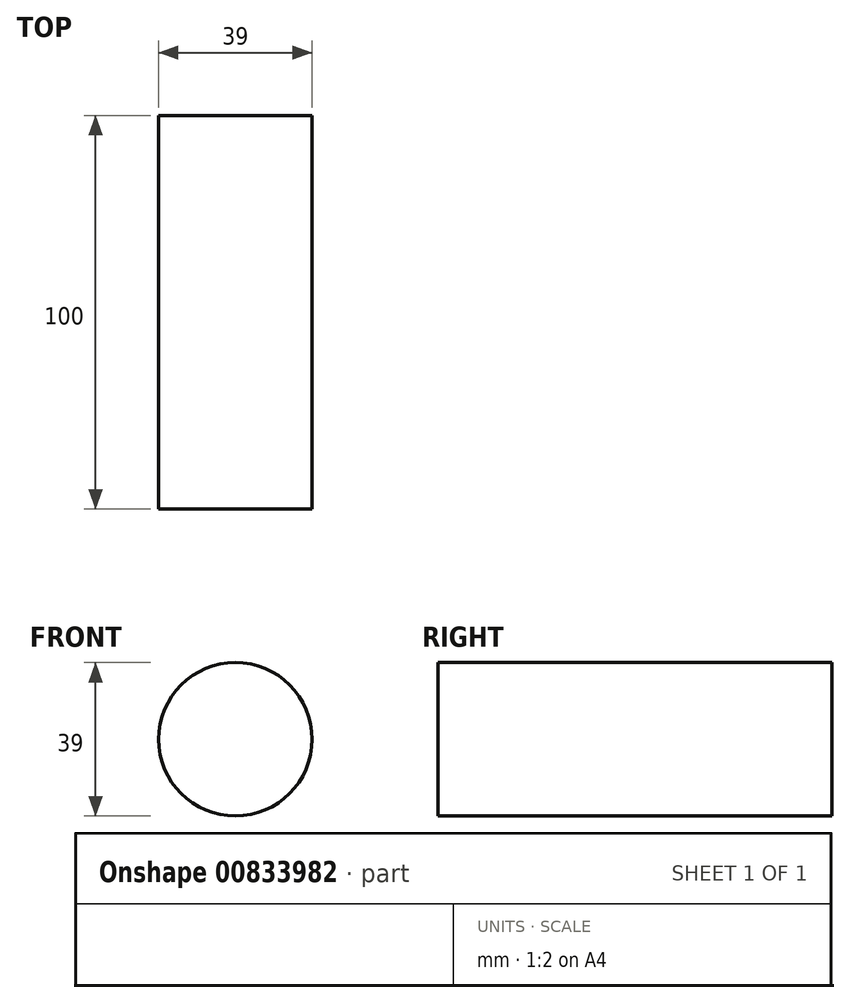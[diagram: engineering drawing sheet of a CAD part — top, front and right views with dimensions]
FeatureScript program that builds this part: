
annotation { "Feature Type Name" : "Feature", "Feature Type Description" : "" }
export const myFeature = defineFeature(function(context is Context, id is Id, definition is map)
    precondition{}
    {
        {
            var Q0;
            Q0=qCreatedBy(makeId("Front.planeOp"),FACE);
            var sketch = newSketch(context, id + "F0", { "sketchPlane" : qUnion([Q0])});
            skCircle(sketch, "E0", {"center": v(0, 0) * mm, "radius": 19.5 * mm});
            skSolve(sketch);
        }
        {
            var Q0;
            Q0=makeQuery(id+"F0.imprint","IMPRINT",FACE,{"disambiguationData":[TD([[makeQuery(id+"F0.imprint","IMPRINT",EDGE,{"derivedFrom":sQuery(id+"F0.wireOp",EDGE,"E0")}),1.0]])]});
            extrude(context, id + "F1", {"entities" : qUnion([Q0]), "depth" : 100 * mm, "offsetDistance" : 25 * mm});
        }
    });
